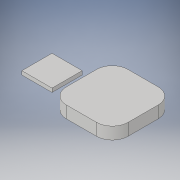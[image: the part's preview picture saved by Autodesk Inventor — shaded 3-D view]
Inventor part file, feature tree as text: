
AUTODESK INVENTOR PART (.ipt)
format: ipt  version: 2018 (Build 220112000, 112)  size: 330,240 bytes
history: native  units: in
note: dims shown in document units (in); Inventor stores cm internally (conversion verified against a paired STEP export)
features: extrude x2, sketch x2
ambient origin geometry x8: Origin, YZ Plane, XZ Plane, XY Plane, X Axis, Y Axis, Z Axis, Center Point
bodies: Solid1 (feature_tree), Solid2 (feature_tree)
feature tree (4):
  extrude  "Extrusion1"  Depth=1.0in
  extrude  "Extrusion2"  Depth=2.042in
  sketch  "Sketch1"  dims[d0=1.0in d1=1.0in]
  sketch  "Sketch2"  dims[d2=0.125in d3=0.0in d4=2.042in d5=2.042in d6=2.0in d7=0.4in d8=0.0in d9=0.522in d10=0.522in]
